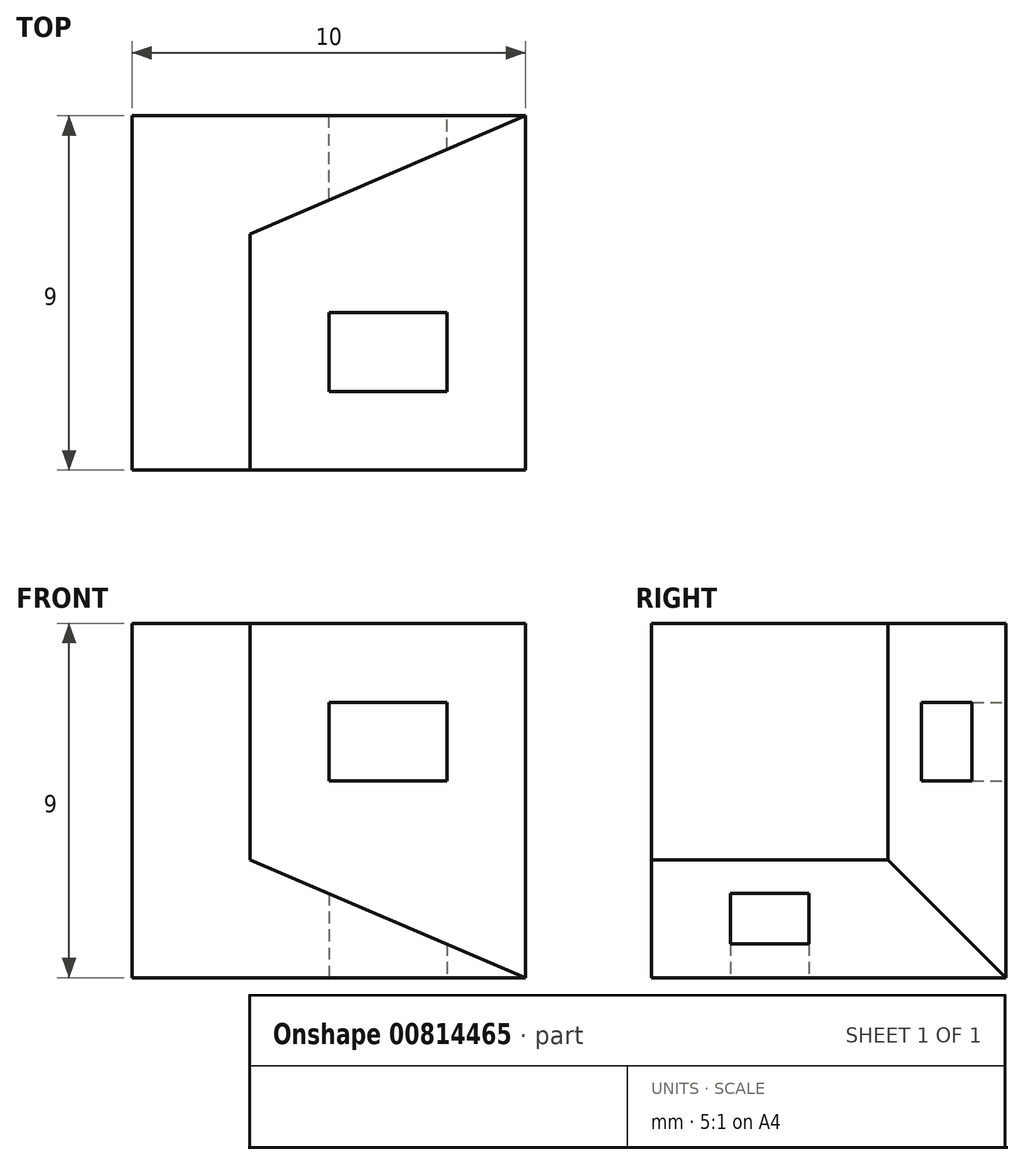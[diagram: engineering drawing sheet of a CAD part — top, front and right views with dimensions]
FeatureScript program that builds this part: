
annotation { "Feature Type Name" : "Feature", "Feature Type Description" : "" }
export const myFeature = defineFeature(function(context is Context, id is Id, definition is map)
    precondition{}
    {
        {
            var Q0;
            Q0=qCreatedBy(makeId("Front.planeOp"),FACE);
            var sketch = newSketch(context, id + "F0", { "sketchPlane" : qUnion([Q0])});
            skLineSegment(sketch, "E0", {"start": v(0, 9) * mm, "end": v(0, 0) * mm});
            skLineSegment(sketch, "E1", {"start": v(0, 0) * mm, "end": v(10, 0) * mm});
            skLineSegment(sketch, "E2", {"start": v(10, 0) * mm, "end": v(3, 3) * mm});
            skLineSegment(sketch, "E3", {"start": v(3, 3) * mm, "end": v(3, 9) * mm});
            skLineSegment(sketch, "E4", {"start": v(3, 9) * mm, "end": v(0, 9) * mm});
            skSolve(sketch);
        }
        {
            var Q0;
            Q0 = qSketchRegion(id + "F0", true);
            extrude(context, id + "F1", {"entities" : qUnion([Q0]), "oppositeDirection" : true, "depth" : 9 * mm, "offsetDistance" : 25 * mm});
        }
        {
            var Q0;
            Q0=makeQuery(id+"F1.opExtrude","SWEPT_FACE",FACE,{"disambiguationData":[OSD([sQuery(id+"F0.wireOp",EDGE,"E4")])]});
            var sketch = newSketch(context, id + "F2", { "sketchPlane" : qUnion([Q0])});
            skLineSegment(sketch, "E5.0.0", {"start": v(0, 0) * mm, "end": v(3, 0) * mm});
            skLineSegment(sketch, "E5.0.1", {"start": v(3, 0) * mm, "end": v(3, 9) * mm});
            skLineSegment(sketch, "E5.0.2", {"start": v(3, 9) * mm, "end": v(0, 9) * mm});
            skLineSegment(sketch, "E5.0.3", {"start": v(0, 9) * mm, "end": v(0, 0) * mm});
            skLineSegment(sketch, "E6.0", {"start": v(10, 9) * mm, "end": v(3, 9) * mm});
            skLineSegment(sketch, "E7", {"start": v(10, 9) * mm, "end": v(3, 6) * mm});
            skSolve(sketch);
        }
        {
            var Q0;
            Q0 = qSketchRegion(id + "F2", true);
            extrude(context, id + "F3", {"entities" : qUnion([Q0]), "operationType" : NewBodyOperationType.ADD, "oppositeDirection" : true, "depth" : 9 * mm, "offsetDistance" : 25 * mm});
        }
        {
            var Q0;
            Q0=makeQuery(id+"F3.boolean.opBoolean","MERGE",FACE,{"derivedFrom":[makeQuery(id+"F1.opExtrude","CAP_FACE",FACE,{"disambiguationData":[OSD([sQuery(id+"F0.wireOp",EDGE,"E0"),sQuery(id+"F0.wireOp",EDGE,"E1"),sQuery(id+"F0.wireOp",EDGE,"E2"),sQuery(id+"F0.wireOp",EDGE,"E3"),sQuery(id+"F0.wireOp",EDGE,"E4")])],"isStart":false}),makeQuery(id+"F3.opExtrude","SWEPT_FACE",FACE,{"disambiguationData":[OSD([sQuery(id+"F2.wireOp",EDGE,"E6.0"),sQuery(id+"F2.wireOp",EDGE,"E5.0.2")])]})]});
            var sketch = newSketch(context, id + "F4", { "sketchPlane" : qUnion([Q0])});
            skLineSegment(sketch, "E8.bottom", {"start": v(-8, 7) * mm, "end": v(-5, 7) * mm});
            skLineSegment(sketch, "E8.top", {"start": v(-8, 5) * mm, "end": v(-5, 5) * mm});
            skLineSegment(sketch, "E8.left", {"start": v(-8, 7) * mm, "end": v(-8, 5) * mm});
            skLineSegment(sketch, "E8.right", {"start": v(-5, 7) * mm, "end": v(-5, 5) * mm});
            skSolve(sketch);
        }
        {
            var Q0;
            Q0 = qSketchRegion(id + "F4", true);
            extrude(context, id + "F5", {"entities" : qUnion([Q0]), "operationType" : NewBodyOperationType.REMOVE, "endBound" : BoundingType.THROUGH_ALL, "oppositeDirection" : true, "depth" : 25 * mm, "offsetDistance" : 25 * mm});
        }
        {
            var Q0;
            Q0=makeQuery(id+"F1.opExtrude","SWEPT_FACE",FACE,{"disambiguationData":[OSD([sQuery(id+"F0.wireOp",EDGE,"E1")])]});
            var sketch = newSketch(context, id + "F6", { "sketchPlane" : qUnion([Q0])});
            skLineSegment(sketch, "E9.bottom", {"start": v(8, -2) * mm, "end": v(5, -2) * mm});
            skLineSegment(sketch, "E9.top", {"start": v(8, -4) * mm, "end": v(5, -4) * mm});
            skLineSegment(sketch, "E9.left", {"start": v(8, -2) * mm, "end": v(8, -4) * mm});
            skLineSegment(sketch, "E9.right", {"start": v(5, -2) * mm, "end": v(5, -4) * mm});
            skSolve(sketch);
        }
        {
            var Q0;
            Q0 = qSketchRegion(id + "F6", true);
            extrude(context, id + "F7", {"entities" : qUnion([Q0]), "operationType" : NewBodyOperationType.REMOVE, "endBound" : BoundingType.THROUGH_ALL, "oppositeDirection" : true, "depth" : 25 * mm, "offsetDistance" : 25 * mm});
        }
    });
